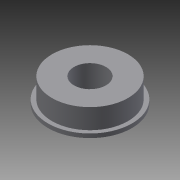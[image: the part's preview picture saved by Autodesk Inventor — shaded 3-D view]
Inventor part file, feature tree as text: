
AUTODESK INVENTOR PART (.ipt)
format: ipt  version: 2013 (Build 170138000, 138)  size: 87,040 bytes
history: native  units: in
note: dims shown in document units (in); Inventor stores cm internally (conversion verified against a paired STEP export)
features: extrude x2, sketch x2
ambient origin geometry x8: Origin, YZ Plane, XZ Plane, XY Plane, X Axis, Y Axis, Z Axis, Center Point
bodies: Solid1 (feature_tree)
feature tree (4):
  extrude  "Extrusion1"  Depth=0.315in
  extrude  "Extrusion2"  Depth=0.748in
  sketch  "Sketch1"  dims[d0=0.8268in d1=0.315in]
  sketch  "Sketch2"  dims[d2=0.0394in d3=0.0in d4=0.748in d5=0.1969in d6=0.0in]
